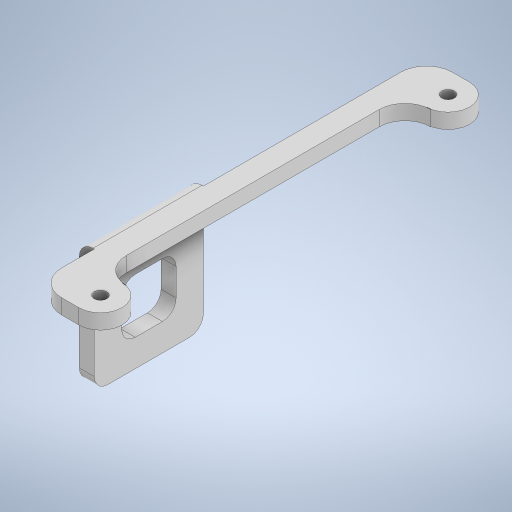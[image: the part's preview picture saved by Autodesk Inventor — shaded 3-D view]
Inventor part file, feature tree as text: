
AUTODESK INVENTOR PART (.ipt)
format: ipt  version: 2023 (Build 270158000, 158)  size: 676,352 bytes
history: native  units: in
note: dims shown in document units (in); Inventor stores cm internally (conversion verified against a paired STEP export)
features: extrude x3, sketch x3, fillet x1
ambient origin geometry x8: Origin, YZ Plane, XZ Plane, XY Plane, X Axis, Y Axis, Z Axis, Center Point
bodies: Solid1 (feature_tree)
feature tree (7):
  extrude  "Extrusion1"  Depth=0.116in
  extrude  "Extrusion2"  Depth=0.395in
  extrude  "Extrusion3"  Depth=0.395in
  fillet  "Fillet1"  Radius=0.2362in
  sketch  "Sketch1"  dims[d0=0.116in d2=0.116in]
  sketch  "Sketch2"  dims[d3=0.395in d4=0.395in]
  sketch  "Sketch4"  dims[d7=3.187in d8=0.395in d9=0.2362in d10=0.2362in d11=0.2362in d12=0.2362in d13=0.1378in d14=0.0in d15=1.81in d16=1.0in d17=1.0in d19=0.25in d22=0.125in d23=0.125in d24=0.125in d25=0.125in d26=0.125in d27=0.125in d28=0.1378in d29=0.0in d30=0.1378in d31=0.0in d32=0.125in]
